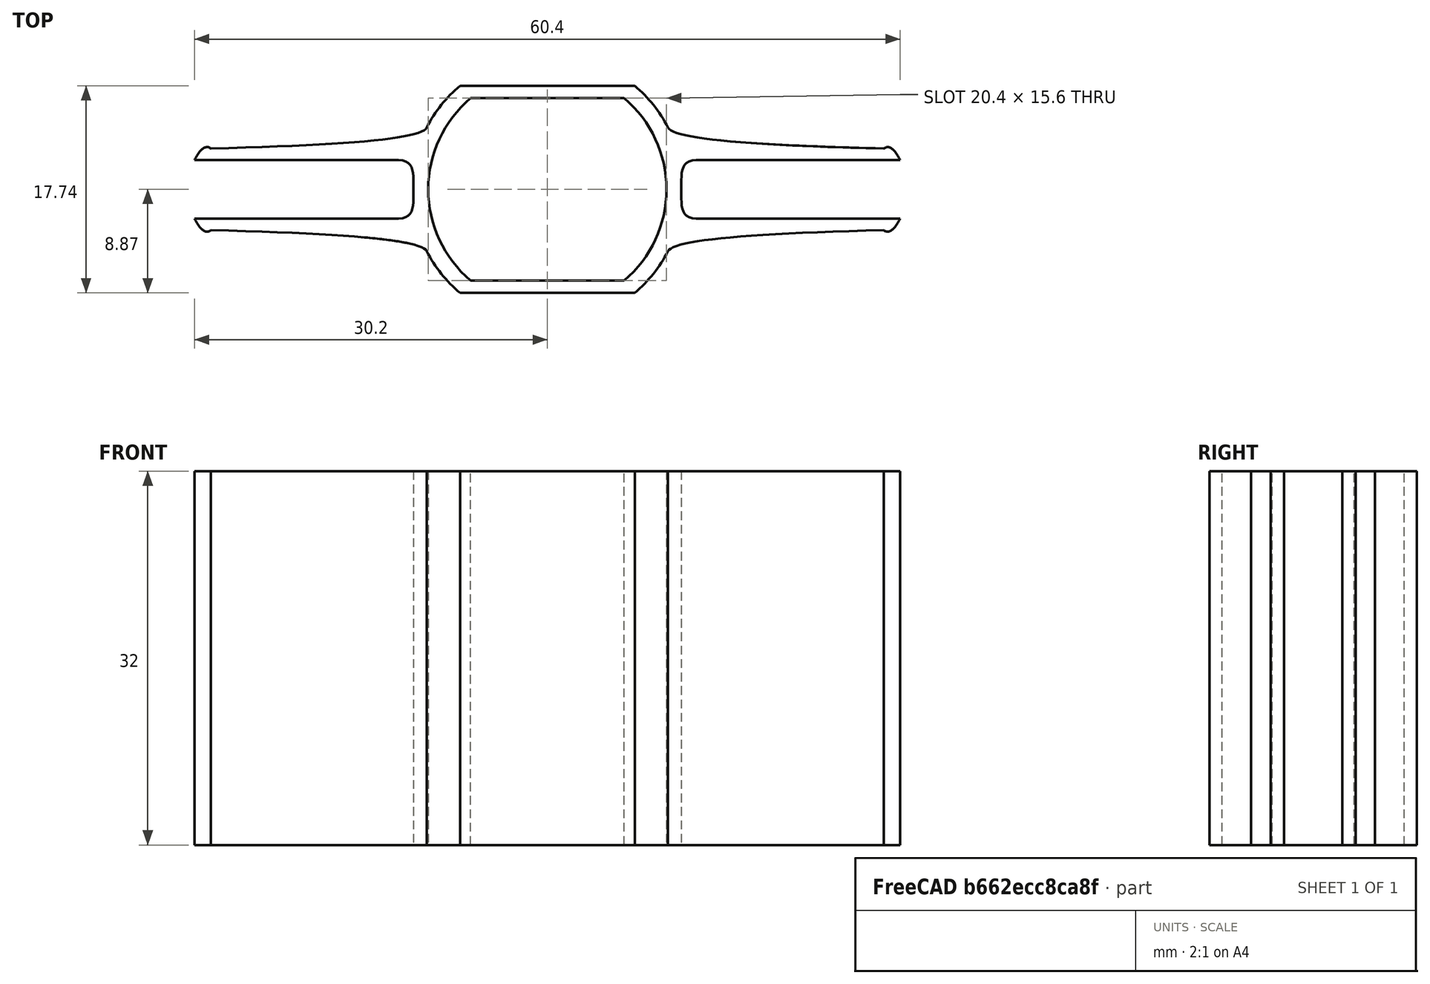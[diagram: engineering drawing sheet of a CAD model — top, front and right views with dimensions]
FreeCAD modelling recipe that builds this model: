
FCSTD DOCUMENT  (FreeCAD 0.19R0.19.2)
Label: 016
License: All rights reserved
LicenseURL: http://en.wikipedia.org/wiki/All_rights_reserved
objects: Sketcher::SketchObject×2, Part::Extrusion×1
note: 3 computed .brp shape members not serialized (recipe doc carries the construction recipe); baked Part::Feature solids carry a one-line shape summary decoded from their .brp

FEATURE [Sketcher::SketchObject] Sketch  label="main001"
  FullyConstrained = true
  sketch-geometry (80):
    g0: ArcOfCircle CenterX=-3.45031e-07 CenterY=0 CenterZ=0 NormalX=0 NormalY=0 NormalZ=1 AngleXU=0 Radius=10.2 StartAngle=5.4126 EndAngle=7.15377
    g1: ArcOfCircle CenterX=-3.45031e-07 CenterY=0 CenterZ=0 NormalX=0 NormalY=0 NormalZ=1 AngleXU=0 Radius=10.2 StartAngle=2.27101 EndAngle=4.01218
    g2: LineSegment StartX=-6.57267 StartY=7.8 StartZ=0 EndX=6.57267 EndY=7.8 EndZ=0
    g3: LineSegment StartX=-6.57267 StartY=-7.8 StartZ=0 EndX=6.57267 EndY=-7.8 EndZ=0
    g4: ArcOfCircle CenterX=-3.45031e-07 CenterY=0 CenterZ=0 NormalX=0 NormalY=0 NormalZ=1 AngleXU=0 Radius=11.6 StartAngle=2.27101 EndAngle=2.66709
    g5: ArcOfCircle CenterX=-3.45031e-07 CenterY=0 CenterZ=0 NormalX=0 NormalY=0 NormalZ=1 AngleXU=0 Radius=11.6 StartAngle=5.4126 EndAngle=5.80868
    g6: LineSegment StartX=-7.4748 StartY=8.87059 StartZ=0 EndX=7.4748 EndY=8.87059 EndZ=0
    g7: LineSegment StartX=-7.4748 StartY=-8.87059 StartZ=0 EndX=7.4748 EndY=-8.87059 EndZ=0
    g8: ArcOfCircle CenterX=-3.45031e-07 CenterY=0 CenterZ=0 NormalX=0 NormalY=0 NormalZ=1 AngleXU=0 Radius=11.6 StartAngle=3.6161 EndAngle=4.01218
    g9: ArcOfCircle CenterX=-3.45031e-07 CenterY=0 CenterZ=0 NormalX=0 NormalY=0 NormalZ=1 AngleXU=0 Radius=11.6 StartAngle=0.474503 EndAngle=0.870585
    g10: Circle CenterX=-28.8 CenterY=3.5 CenterZ=0 NormalX=0 NormalY=0 NormalZ=1 AngleXU=0 Radius=1
    g11: Circle CenterX=-10.9247 CenterY=3.9 CenterZ=0 NormalX=0 NormalY=0 NormalZ=1 AngleXU=0 Radius=1
    g12: Circle CenterX=-10.3184 CenterY=5.3 CenterZ=0 NormalX=0 NormalY=0 NormalZ=1 AngleXU=0 Radius=1
    g13: BSplineCurve PolesCount=3 KnotsCount=2 Degree=2 IsPeriodic=0
    g14: GeomPoint X=-28.8 Y=3.5 Z=0
    g15: GeomPoint X=-10.3184 Y=5.3 Z=0
    g16: Circle CenterX=28.8 CenterY=3.5 CenterZ=0 NormalX=0 NormalY=0 NormalZ=1 AngleXU=0 Radius=1
    g17: Circle CenterX=10.9247 CenterY=3.9 CenterZ=0 NormalX=0 NormalY=0 NormalZ=1 AngleXU=0 Radius=1
    g18: Circle CenterX=10.3184 CenterY=5.3 CenterZ=0 NormalX=0 NormalY=0 NormalZ=1 AngleXU=0 Radius=1
    g19: BSplineCurve PolesCount=3 KnotsCount=2 Degree=2 IsPeriodic=0
    g20: GeomPoint X=28.8 Y=3.5 Z=0
    g21: GeomPoint X=10.3184 Y=5.3 Z=0
    g22: Circle CenterX=-28.8 CenterY=-3.5 CenterZ=0 NormalX=0 NormalY=0 NormalZ=1 AngleXU=0 Radius=1
    g23: Circle CenterX=-10.9247 CenterY=-3.9 CenterZ=0 NormalX=0 NormalY=0 NormalZ=1 AngleXU=0 Radius=1
    g24: Circle CenterX=-10.3184 CenterY=-5.3 CenterZ=0 NormalX=0 NormalY=0 NormalZ=1 AngleXU=0 Radius=1
    g25: BSplineCurve PolesCount=3 KnotsCount=2 Degree=2 IsPeriodic=0
    g26: GeomPoint X=-28.8 Y=-3.5 Z=0
    g27: GeomPoint X=-10.3184 Y=-5.3 Z=0
    g28: Circle CenterX=28.8 CenterY=-3.5 CenterZ=0 NormalX=0 NormalY=0 NormalZ=1 AngleXU=0 Radius=1
    g29: Circle CenterX=10.9247 CenterY=-3.9 CenterZ=0 NormalX=0 NormalY=0 NormalZ=1 AngleXU=0 Radius=1
    g30: Circle CenterX=10.3184 CenterY=-5.3 CenterZ=0 NormalX=0 NormalY=0 NormalZ=1 AngleXU=0 Radius=1
    g31: BSplineCurve PolesCount=3 KnotsCount=2 Degree=2 IsPeriodic=0
    g32: GeomPoint X=28.8 Y=-3.5 Z=0
    g33: GeomPoint X=10.3184 Y=-5.3 Z=0
    g34-g38: Circle x5 (B-spline internal-alignment scaffolding for g39; pole/knot coordinates omitted)
    g39: BSplineCurve PolesCount=5 KnotsCount=3 Degree=3 IsPeriodic=0
    g40: GeomPoint X=12.7274 Y=2.5 Z=0
    g41: GeomPoint X=11.4637 Y=2.49999e-07 Z=0
    g42: GeomPoint X=12.7274 Y=-2.5 Z=0
    g43-g47: Circle x5 (B-spline internal-alignment scaffolding for g48; pole/knot coordinates omitted)
    g48: BSplineCurve PolesCount=5 KnotsCount=3 Degree=3 IsPeriodic=0
    g49: GeomPoint X=-12.7274 Y=2.5 Z=0
    g50: GeomPoint X=-11.4637 Y=2.50004e-07 Z=0
    g51: GeomPoint X=-12.7274 Y=-2.5 Z=0
    g52: LineSegment StartX=-30.2 StartY=-2.5 StartZ=0 EndX=-12.7274 EndY=-2.5 EndZ=0
    g53: LineSegment StartX=-30.2 StartY=2.5 StartZ=0 EndX=-12.7274 EndY=2.5 EndZ=0
    g54: LineSegment StartX=30.2 StartY=2.5 StartZ=0 EndX=12.7274 EndY=2.5 EndZ=0
    g55: LineSegment StartX=30.2 StartY=-2.5 StartZ=0 EndX=12.7274 EndY=-2.5 EndZ=0
    g56: Circle CenterX=-30.2 CenterY=2.5 CenterZ=0 NormalX=0 NormalY=0 NormalZ=1 AngleXU=0 Radius=1
    g57: Circle CenterX=-29.4304 CenterY=3.99253 CenterZ=0 NormalX=0 NormalY=0 NormalZ=1 AngleXU=0 Radius=1
    g58: Circle CenterX=-28.8 CenterY=3.5 CenterZ=0 NormalX=0 NormalY=0 NormalZ=1 AngleXU=0 Radius=1
    g59: BSplineCurve PolesCount=3 KnotsCount=2 Degree=2 IsPeriodic=0
    g60: GeomPoint X=-30.2 Y=2.5 Z=0
    g61: GeomPoint X=-28.8 Y=3.5 Z=0
    g62: Circle CenterX=30.2 CenterY=-2.5 CenterZ=0 NormalX=0 NormalY=0 NormalZ=1 AngleXU=0 Radius=1
    g63: Circle CenterX=29.4304 CenterY=-3.99253 CenterZ=0 NormalX=0 NormalY=0 NormalZ=1 AngleXU=0 Radius=1
    g64: Circle CenterX=28.8 CenterY=-3.5 CenterZ=0 NormalX=0 NormalY=0 NormalZ=1 AngleXU=0 Radius=1
    g65: BSplineCurve PolesCount=3 KnotsCount=2 Degree=2 IsPeriodic=0
    g66: GeomPoint X=30.2 Y=-2.5 Z=0
    g67: GeomPoint X=28.8 Y=-3.5 Z=0
    g68: Circle CenterX=30.2 CenterY=2.5 CenterZ=0 NormalX=0 NormalY=0 NormalZ=1 AngleXU=0 Radius=1
    g69: Circle CenterX=29.4304 CenterY=3.99253 CenterZ=0 NormalX=0 NormalY=0 NormalZ=1 AngleXU=0 Radius=1
    g70: Circle CenterX=28.8 CenterY=3.5 CenterZ=0 NormalX=0 NormalY=0 NormalZ=1 AngleXU=0 Radius=1
    g71: BSplineCurve PolesCount=3 KnotsCount=2 Degree=2 IsPeriodic=0
    g72: GeomPoint X=30.2 Y=2.5 Z=0
    g73: GeomPoint X=28.8 Y=3.5 Z=0
    g74: Circle CenterX=-30.2 CenterY=-2.5 CenterZ=0 NormalX=0 NormalY=0 NormalZ=1 AngleXU=0 Radius=1
    g75: Circle CenterX=-29.4304 CenterY=-3.99253 CenterZ=0 NormalX=0 NormalY=0 NormalZ=1 AngleXU=0 Radius=1
    g76: Circle CenterX=-28.8 CenterY=-3.5 CenterZ=0 NormalX=0 NormalY=0 NormalZ=1 AngleXU=0 Radius=1
    g77: BSplineCurve PolesCount=3 KnotsCount=2 Degree=2 IsPeriodic=0
    g78: GeomPoint X=-30.2 Y=-2.5 Z=0
    g79: GeomPoint X=-28.8 Y=-3.5 Z=0
  constraints (131):
    c: Block(g0)
    c: Equal(g0,g1)
    c: Coincident(g0,g1)
    c: Coincident(g2,g1)
    c: Coincident(g2,g0)
    c: Horizontal(g2)
    c: Coincident(g3,g1)
    c: Coincident(g3,g0)
    c: Horizontal(g3)
    c: Block(g2)
    c: Block(g3)
    c: Coincident(g4,g0)
    c: Coincident(g5,g0)
    c: Block(g5)
    c: Block(g4)
    c: Coincident(g6,g4)
    c: Coincident(g6,g9)
    c: Horizontal(g6)
    c: Coincident(g7,g8)
    c: Coincident(g7,g5)
    c: Horizontal(g7)
    c: Equal(g4,g8)
    c: Coincident(g4,g8)
    c: Equal(g5,g9)
    c: Coincident(g5,g9)
    c: Block(g8)
    c: Block(g9)
    c: Weight(g10) = 1
    c: Equal(g10,g11)
    c: Equal(g10,g12)
    c: Coincident(g13,g4)
    c: InternalAlignment(g10,g13)
    c: InternalAlignment(g11,g13)
    c: InternalAlignment(g12,g13)
    c: InternalAlignment(g14,g13)
    c: InternalAlignment(g15,g13)
    c: Weight(g16) = 1
    c: Equal(g16,g17)
    c: Equal(g16,g18)
    c: Coincident(g19,g9)
    c: InternalAlignment(g16,g19)
    c: InternalAlignment(g17,g19)
    c: InternalAlignment(g18,g19)
    c: InternalAlignment(g20,g19)
    c: InternalAlignment(g21,g19)
    c: Weight(g22) = 1
    c: Equal(g22,g23)
    c: Equal(g22,g24)
    c: Coincident(g25,g8)
    c: InternalAlignment(g22,g25)
    c: InternalAlignment(g23,g25)
    c: InternalAlignment(g24,g25)
    c: InternalAlignment(g26,g25)
    c: InternalAlignment(g27,g25)
    c: Weight(g28) = 1
    c: Equal(g28,g29)
    c: Equal(g28,g30)
    c: Coincident(g31,g5)
    c: InternalAlignment(g28,g31)
    c: InternalAlignment(g29,g31)
    c: InternalAlignment(g30,g31)
    c: InternalAlignment(g32,g31)
    c: InternalAlignment(g33,g31)
    c: Block(g19)
    c: Block(g13)
    c: Block(g31)
    c: Block(g25)
    c: Weight(g34) = 1
    c: Equal(g34, g35-g38) x4
    c: InternalAlignment(g34-g38 -> g39) x5
    c: InternalAlignment(g40,g39)
    c: InternalAlignment(g41,g39)
    c: InternalAlignment(g42,g39)
    c: Weight(g43) = 1
    c: Equal(g43,g44)
    c: Equal(g43,g45)
    c: Equal(g43,g46)
    c: InternalAlignment(g43-g47 -> g48) x5
    c: InternalAlignment(g49,g48)
    c: InternalAlignment(g50,g48)
    c: InternalAlignment(g51,g48)
    c: Block(g48)
    c: Block(g39)
    c: Coincident(g52,g48)
    c: Tangent(g52,g22)
    c: Coincident(g53,g48)
    c: Tangent(g53,g10)
    c: Coincident(g54,g39)
    c: Tangent(g54,g16)
    c: Coincident(g55,g39)
    c: Tangent(g55,g28)
    c: Weight(g56) = 1
    c: Equal(g56,g57)
    c: Equal(g56,g58)
    c: InternalAlignment(g56,g59)
    c: InternalAlignment(g57,g59)
    c: InternalAlignment(g58,g59)
    c: InternalAlignment(g60,g59)
    c: InternalAlignment(g61,g59)
    c: Weight(g62) = 1
    c: Equal(g62,g63)
    c: Equal(g62,g64)
    c: InternalAlignment(g62,g65)
    c: InternalAlignment(g63,g65)
    c: InternalAlignment(g64,g65)
    c: InternalAlignment(g66,g65)
    c: InternalAlignment(g67,g65)
    c: Weight(g68) = 1
    c: Equal(g68,g69)
    c: Equal(g68,g70)
    c: InternalAlignment(g68,g71)
    c: InternalAlignment(g69,g71)
    c: InternalAlignment(g70,g71)
    c: InternalAlignment(g72,g71)
    c: InternalAlignment(g73,g71)
    c: Block(g71)
    c: Block(g54)
    c: Block(g65)
    c: Block(g55)
    c: Weight(g74) = 1
    c: Equal(g74,g75)
    c: Equal(g74,g76)
    c: InternalAlignment(g74,g77)
    c: InternalAlignment(g75,g77)
    c: InternalAlignment(g76,g77)
    c: InternalAlignment(g78,g77)
    c: InternalAlignment(g79,g77)
    c: Block(g77)
    c: Block(g52)
    c: Block(g59)
    c: Block(g53)
FEATURE [Part::Extrusion] Extrude  label="main"
  Base = -> Sketch
  Dir = (0,0,1)
  DirMode = 2
  FaceMakerClass = Part::FaceMakerBullseye
  LengthFwd = 32
  LengthRev = 0
  Solid = true
  Symmetric = false
FEATURE [Sketcher::SketchObject] Sketch001  label="mainCollingAndStructuralHoles"
  FullyConstrained = true
  Placement = pos=(0,0,0) rot=(-1,0,0;4.71239rad)
  sketch-geometry (6):
    g0: LineSegment StartX=0 StartY=0 StartZ=0 EndX=5 EndY=0 EndZ=0
    g1: LineSegment StartX=0 StartY=0 StartZ=0 EndX=-5 EndY=0 EndZ=0
    g2: LineSegment StartX=5 StartY=0 StartZ=0 EndX=3 EndY=0 EndZ=0
    g3: LineSegment StartX=-5 StartY=0 StartZ=0 EndX=-3 EndY=0 EndZ=0
    g4: LineSegment StartX=-5 StartY=0 StartZ=0 EndX=-5 EndY=2 EndZ=0
    g5: LineSegment StartX=5 StartY=0 StartZ=0 EndX=5 EndY=2 EndZ=0
  constraints (18):
    c: Horizontal(g0)
    c: Distance(g0) = 5
    c: Coincident(g1,g0)
    c: Horizontal(g1)
    c: Distance(g1) = 5
    c: Coincident(g0,g-1)
    c: Horizontal(g2)
    c: Distance(g2) = 2
    c: Horizontal(g3)
    c: Distance(g3) = 2
    c: Vertical(g4)
    c: Distance(g4) = 2
    c: Vertical(g5)
    c: Equal(g4,g5) = 2
    c: Coincident(g5,g0)
    c: Coincident(g2,g0)
    c: Coincident(g3,g1)
    c: Coincident(g4,g1)
